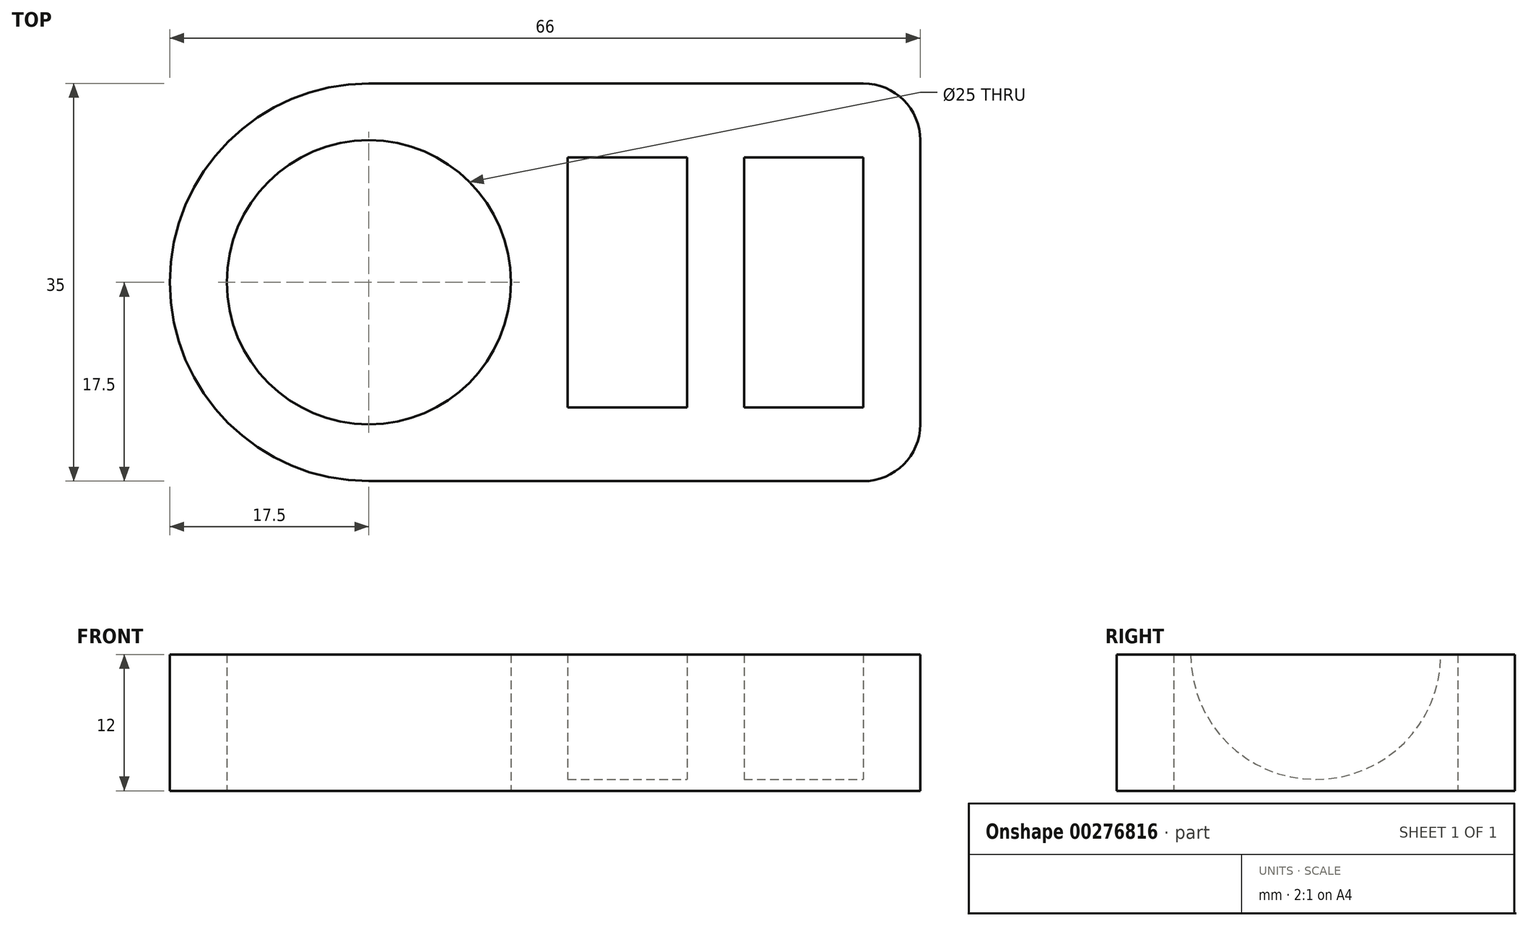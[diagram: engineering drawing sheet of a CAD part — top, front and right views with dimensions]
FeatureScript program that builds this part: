
annotation { "Feature Type Name" : "Feature", "Feature Type Description" : "" }
export const myFeature = defineFeature(function(context is Context, id is Id, definition is map)
    precondition{}
    {
        {
            var Q0;
            Q0=qCreatedBy(makeId("Top.planeOp"),FACE);
            var sketch = newSketch(context, id + "F0", { "sketchPlane" : qUnion([Q0])});
            skLineSegment(sketch, "E0.bottom", {"start": v(17.5, 0) * mm, "end": v(61, 0) * mm});
            skLineSegment(sketch, "E0.top", {"start": v(17.5, 35) * mm, "end": v(61, 35) * mm});
            skLineSegment(sketch, "E0.left", {"start": v(0, 17.5) * mm, "end": v(0, 17.5) * mm});
            skLineSegment(sketch, "E0.right", {"start": v(66, 5) * mm, "end": v(66, 30) * mm});
            skLineSegment(sketch, "E1.bottom", {"start": v(0, 0) * mm, "end": v(17.5, 0) * mm, "construction": true});
            skLineSegment(sketch, "E1.top", {"start": v(0, 17.5) * mm, "end": v(17.5, 17.5) * mm, "construction": true});
            skLineSegment(sketch, "E1.left", {"start": v(0, 0) * mm, "end": v(0, 17.5) * mm, "construction": true});
            skLineSegment(sketch, "E1.right", {"start": v(17.5, 0) * mm, "end": v(17.5, 17.5) * mm, "construction": true});
            skCircle(sketch, "E2", {"center": v(17.5, 17.5) * mm, "radius": 12.5 * mm});
            skPoint(sketch, "E3.visualSharp", {"position": v(0, 0) * mm});
            skArc(sketch, "E3.filletArc", {"start": v(0, 17.5) * mm, "mid": v(5.13, 5.13) * mm, "end": v(17.5, 0) * mm});
            skPoint(sketch, "E4.visualSharp", {"position": v(0, 35) * mm});
            skArc(sketch, "E4.filletArc", {"start": v(17.5, 35) * mm, "mid": v(5.13, 29.87) * mm, "end": v(0, 17.5) * mm});
            skPoint(sketch, "E5.visualSharp", {"position": v(66, 35) * mm});
            skArc(sketch, "E5.filletArc", {"start": v(66, 30) * mm, "mid": v(64.54, 33.54) * mm, "end": v(61, 35) * mm});
            skPoint(sketch, "E6.visualSharp", {"position": v(66, 0) * mm});
            skArc(sketch, "E6.filletArc", {"start": v(61, 0) * mm, "mid": v(64.54, 1.46) * mm, "end": v(66, 5) * mm});
            skSolve(sketch);
        }
        {
            var Q0;
            Q0=makeQuery(id+"F0.imprint","IMPRINT",FACE,{"disambiguationData":[TD([[makeQuery(id+"F0.imprint","IMPRINT",EDGE,{"derivedFrom":sQuery(id+"F0.wireOp",EDGE,"E0.bottom")}),1.0]])]});
            extrude(context, id + "F1", {"entities" : qUnion([Q0]), "depth" : 12 * mm});
        }
        {
            var Q0;
            Q0=makeQuery(id+"F1.opExtrude","CAP_FACE",FACE,{"disambiguationData":[OSD([sQuery(id+"F0.wireOp",EDGE,"E0.bottom"),sQuery(id+"F0.wireOp",EDGE,"E0.top"),sQuery(id+"F0.wireOp",EDGE,"E0.right"),sQuery(id+"F0.wireOp",EDGE,"E2"),sQuery(id+"F0.wireOp",EDGE,"E3.filletArc"),sQuery(id+"F0.wireOp",EDGE,"E4.filletArc"),sQuery(id+"F0.wireOp",EDGE,"E5.filletArc"),sQuery(id+"F0.wireOp",EDGE,"E6.filletArc")])],"isStart":false});
            var sketch = newSketch(context, id + "F2", { "sketchPlane" : qUnion([Q0])});
            skLineSegment(sketch, "E7.bottom", {"start": v(0, 0) * mm, "end": v(35, 0) * mm, "construction": true});
            skLineSegment(sketch, "E7.top", {"start": v(0, 17.5) * mm, "end": v(35, 17.5) * mm, "construction": true});
            skLineSegment(sketch, "E7.left", {"start": v(0, 0) * mm, "end": v(0, 17.5) * mm, "construction": true});
            skLineSegment(sketch, "E7.right", {"start": v(35, 0) * mm, "end": v(35, 17.5) * mm, "construction": true});
            skLineSegment(sketch, "E8.bottom", {"start": v(35, 17.5) * mm, "end": v(45.5, 17.5) * mm});
            skLineSegment(sketch, "E8.top", {"start": v(35, 6.5) * mm, "end": v(45.5, 6.5) * mm});
            skLineSegment(sketch, "E8.left", {"start": v(35, 17.5) * mm, "end": v(35, 6.5) * mm});
            skLineSegment(sketch, "E8.right", {"start": v(45.5, 17.5) * mm, "end": v(45.5, 6.5) * mm});
            skLineSegment(sketch, "E9", {"start": v(45.5, 17.5) * mm, "end": v(50.5, 17.5) * mm, "construction": true});
            skLineSegment(sketch, "E10.bottom", {"start": v(50.5, 17.5) * mm, "end": v(61, 17.5) * mm});
            skLineSegment(sketch, "E10.top", {"start": v(50.5, 6.5) * mm, "end": v(61, 6.5) * mm});
            skLineSegment(sketch, "E10.left", {"start": v(50.5, 17.5) * mm, "end": v(50.5, 6.5) * mm});
            skLineSegment(sketch, "E10.right", {"start": v(61, 17.5) * mm, "end": v(61, 6.5) * mm});
            skSolve(sketch);
        }
        {
            var Q0;
            Q0=qSketchRegion(id+"F2",true);
            var Q1;
            Q1=sQuery(id+"F2.wireOp",EDGE,"E8.bottom");
            revolve(context, id + "F3", {"operationType" : NewBodyOperationType.REMOVE, "entities" : qUnion([Q0]), "axis" : qUnion([Q1]), "revolveType" : RevolveType.FULL, "oppositeDirection" : true});
        }
    });
